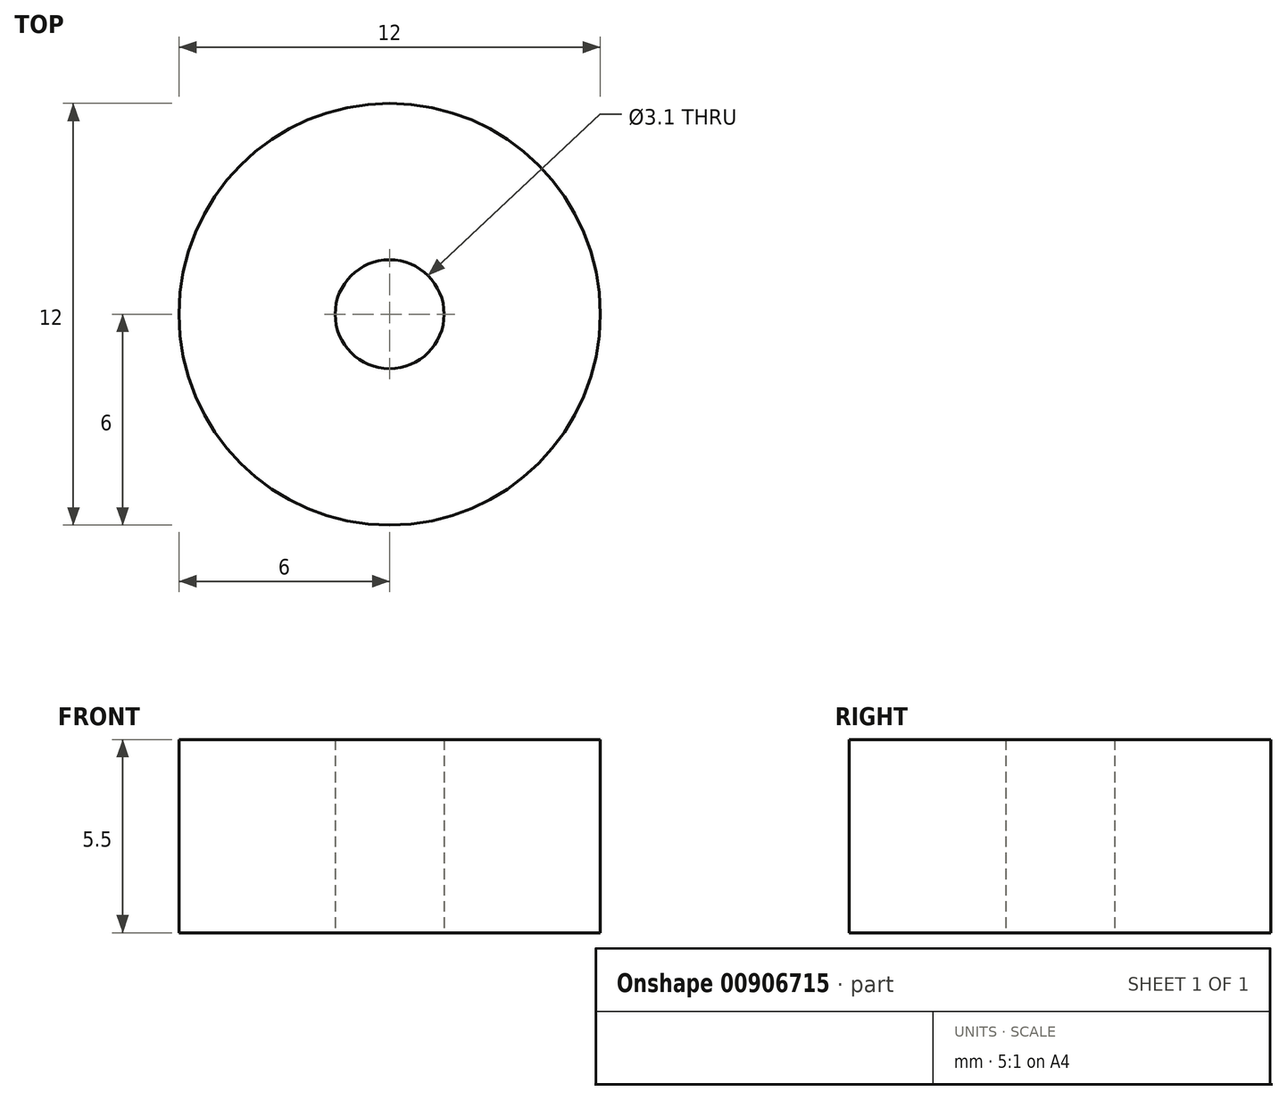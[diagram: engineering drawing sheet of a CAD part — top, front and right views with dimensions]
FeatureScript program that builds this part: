
annotation { "Feature Type Name" : "Feature", "Feature Type Description" : "" }
export const myFeature = defineFeature(function(context is Context, id is Id, definition is map)
    precondition{}
    {
        {
            var Q0;
            Q0=qCreatedBy(makeId("Top.planeOp"),FACE);
            var sketch = newSketch(context, id + "F0", { "sketchPlane" : qUnion([Q0])});
            skCircle(sketch, "E0", {"center": v(0, 0) * mm, "radius": 6 * mm});
            skCircle(sketch, "E1", {"center": v(0, 0) * mm, "radius": 1.55 * mm});
            skSolve(sketch);
        }
        {
            var Q0;
            Q0=makeQuery(id+"F0.imprint","IMPRINT",FACE,{"disambiguationData":[TD([[makeQuery(id+"F0.imprint","IMPRINT",EDGE,{"derivedFrom":sQuery(id+"F0.wireOp",EDGE,"E0")}),1.0]])]});
            extrude(context, id + "F1", {"entities" : qUnion([Q0]), "depth" : 5.5 * mm, "offsetDistance" : 25 * mm});
        }
    });
